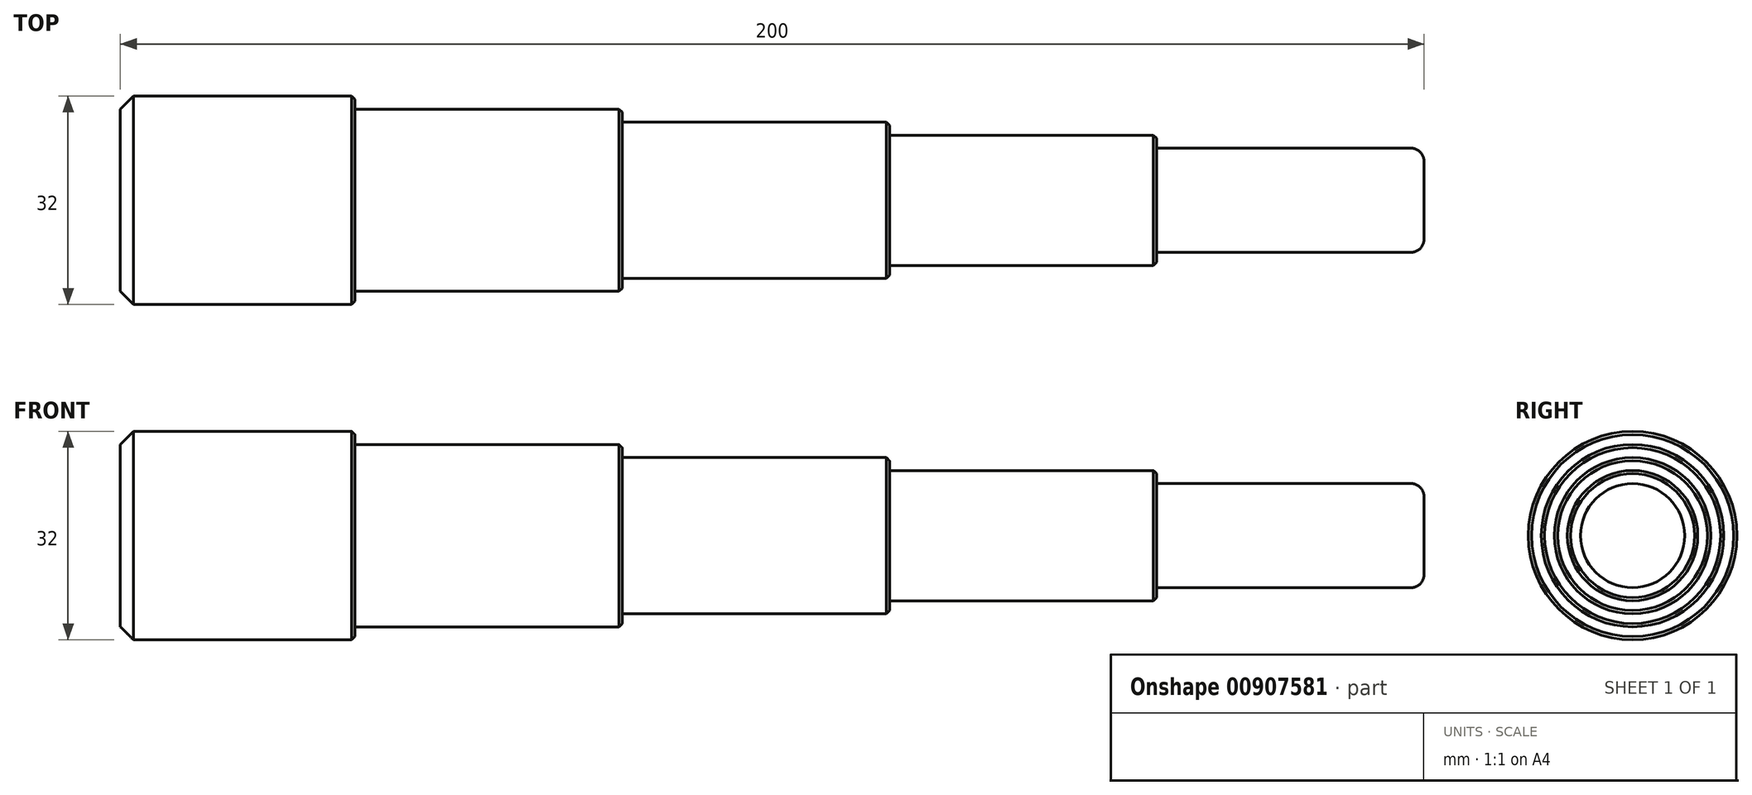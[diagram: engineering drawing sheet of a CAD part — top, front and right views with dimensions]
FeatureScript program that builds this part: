
annotation { "Feature Type Name" : "Feature", "Feature Type Description" : "" }
export const myFeature = defineFeature(function(context is Context, id is Id, definition is map)
    precondition{}
    {
        {
            var Q0;
            Q0=qCreatedBy(makeId("Front.planeOp"),FACE);
            var sketch = newSketch(context, id + "F0", { "sketchPlane" : qUnion([Q0])});
            skLineSegment(sketch, "E0", {"start": v(0, 0) * mm, "end": v(-200, 0) * mm});
            skLineSegment(sketch, "E1", {"start": v(-200, 0) * mm, "end": v(-200, 16) * mm});
            skLineSegment(sketch, "E2", {"start": v(-200, 16) * mm, "end": v(-164, 16) * mm});
            skLineSegment(sketch, "E3", {"start": v(-164, 16) * mm, "end": v(-164, 14) * mm});
            skLineSegment(sketch, "E4", {"start": v(-164, 14) * mm, "end": v(-123, 14) * mm});
            skLineSegment(sketch, "E5", {"start": v(-123, 14) * mm, "end": v(-123, 12) * mm});
            skLineSegment(sketch, "E6", {"start": v(-123, 12) * mm, "end": v(-82, 12) * mm});
            skLineSegment(sketch, "E7", {"start": v(-82, 10) * mm, "end": v(-41, 10) * mm});
            skLineSegment(sketch, "E8", {"start": v(-41, 10) * mm, "end": v(-41, 8) * mm});
            skLineSegment(sketch, "E9", {"start": v(-41, 8) * mm, "end": v(0, 8) * mm});
            skLineSegment(sketch, "E10", {"start": v(0, 8) * mm, "end": v(0, 0) * mm});
            skLineSegment(sketch, "E11", {"start": v(-82, 12) * mm, "end": v(-82, 10) * mm});
            skSolve(sketch);
        }
        {
            var Q0;
            Q0=makeQuery(id+"F0.imprint","IMPRINT",FACE,{"disambiguationData":[TD([[makeQuery(id+"F0.imprint","IMPRINT",EDGE,{"derivedFrom":sQuery(id+"F0.wireOp",EDGE,"E0")}),-1.0]])]});
            var Q1;
            Q1=sQuery(id+"F0.wireOp",EDGE,"E0");
            revolve(context, id + "F1", {"surfaceOperationType" : NewSurfaceOperationType.NEW, "entities" : qUnion([Q0]), "axis" : qUnion([Q1]), "revolveType" : RevolveType.FULL});
        }
        {
            var Q0;
            Q0=makeQuery(id+"F1.opRevolve","SWEPT_EDGE",EDGE,{"disambiguationData":[OSD([sQuery(id+"F0.wireOp",EDGE,"E1"),sQuery(id+"F0.wireOp",EDGE,"E2")])]});
            chamfer(context, id + "F2", {"entities" : qUnion([Q0]), "width" : 2 * mm, "tangentPropagation" : true});
        }
        {
            var Q0;
            Q0=makeQuery(id+"F1.opRevolve","SWEPT_EDGE",EDGE,{"disambiguationData":[OSD([sQuery(id+"F0.wireOp",EDGE,"E2"),sQuery(id+"F0.wireOp",EDGE,"E3")])]});
            var Q1;
            Q1=makeQuery(id+"F1.opRevolve","SWEPT_EDGE",EDGE,{"disambiguationData":[OSD([sQuery(id+"F0.wireOp",EDGE,"E4"),sQuery(id+"F0.wireOp",EDGE,"E5")])]});
            var Q2;
            Q2=makeQuery(id+"F1.opRevolve","SWEPT_EDGE",EDGE,{"disambiguationData":[OSD([sQuery(id+"F0.wireOp",EDGE,"E6"),sQuery(id+"F0.wireOp",EDGE,"E11")])]});
            var Q3;
            Q3=makeQuery(id+"F1.opRevolve","SWEPT_EDGE",EDGE,{"disambiguationData":[OSD([sQuery(id+"F0.wireOp",EDGE,"E7"),sQuery(id+"F0.wireOp",EDGE,"E8")])]});
            chamfer(context, id + "F3", {"entities" : qUnion([Q0, Q1, Q2, Q3]), "width" : 0.5 * mm, "tangentPropagation" : true});
        }
        {
            var Q0;
            Q0=makeQuery(id+"F1.opRevolve","SWEPT_FACE",FACE,{"disambiguationData":[OSD([sQuery(id+"F0.wireOp",EDGE,"E10")])]});
            fillet(context, id + "F4", {"entities" : qUnion([Q0]), "radius" : 2 * mm, "tangentPropagation" : true, "allowEdgeOverflow" : false});
        }
    });
